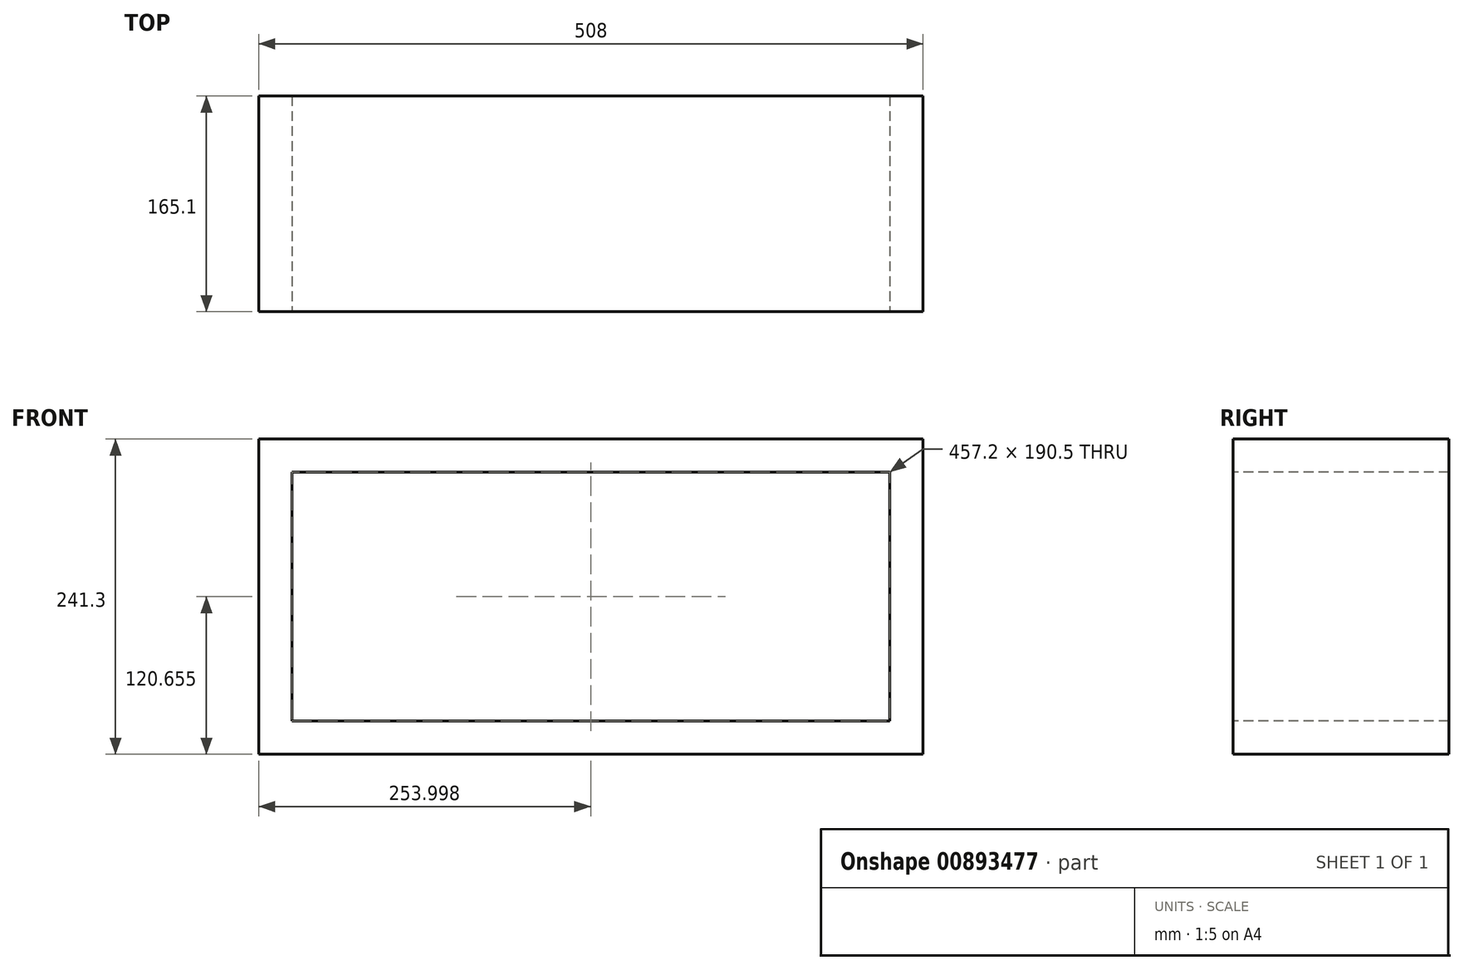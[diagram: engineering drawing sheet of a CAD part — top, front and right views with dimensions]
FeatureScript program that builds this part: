
annotation { "Feature Type Name" : "Feature", "Feature Type Description" : "" }
export const myFeature = defineFeature(function(context is Context, id is Id, definition is map)
    precondition{}
    {
        {
            var Q0;
            Q0=qCreatedBy(makeId("Front.planeOp"),FACE);
            var sketch = newSketch(context, id + "F0", { "sketchPlane" : qUnion([Q0])});
            skLineSegment(sketch, "E0", {"start": v(-237.53, 129.14) * mm, "end": v(219.67, 129.14) * mm});
            skLineSegment(sketch, "E1", {"start": v(-237.53, 129.14) * mm, "end": v(-237.53, -61.36) * mm});
            skLineSegment(sketch, "E2", {"start": v(219.67, 129.14) * mm, "end": v(219.67, -61.36) * mm});
            skLineSegment(sketch, "E3", {"start": v(-237.53, -61.36) * mm, "end": v(219.67, -61.36) * mm});
            skLineSegment(sketch, "E4", {"start": v(-262.93, 154.54) * mm, "end": v(-262.93, -86.76) * mm});
            skLineSegment(sketch, "E5", {"start": v(-262.93, 154.54) * mm, "end": v(245.07, 154.54) * mm});
            skLineSegment(sketch, "E6", {"start": v(245.07, 154.54) * mm, "end": v(245.07, -86.76) * mm});
            skLineSegment(sketch, "E7", {"start": v(-262.93, -86.76) * mm, "end": v(245.07, -86.76) * mm});
            skSolve(sketch);
        }
        {
            var Q0;
            Q0 = qSketchRegion(id + "F0", true);
            extrude(context, id + "F1", {"entities" : qUnion([Q0]), "oppositeDirection" : true, "depth" : 165.1 * mm, "offsetDistance" : 25 * mm});
        }
    });
